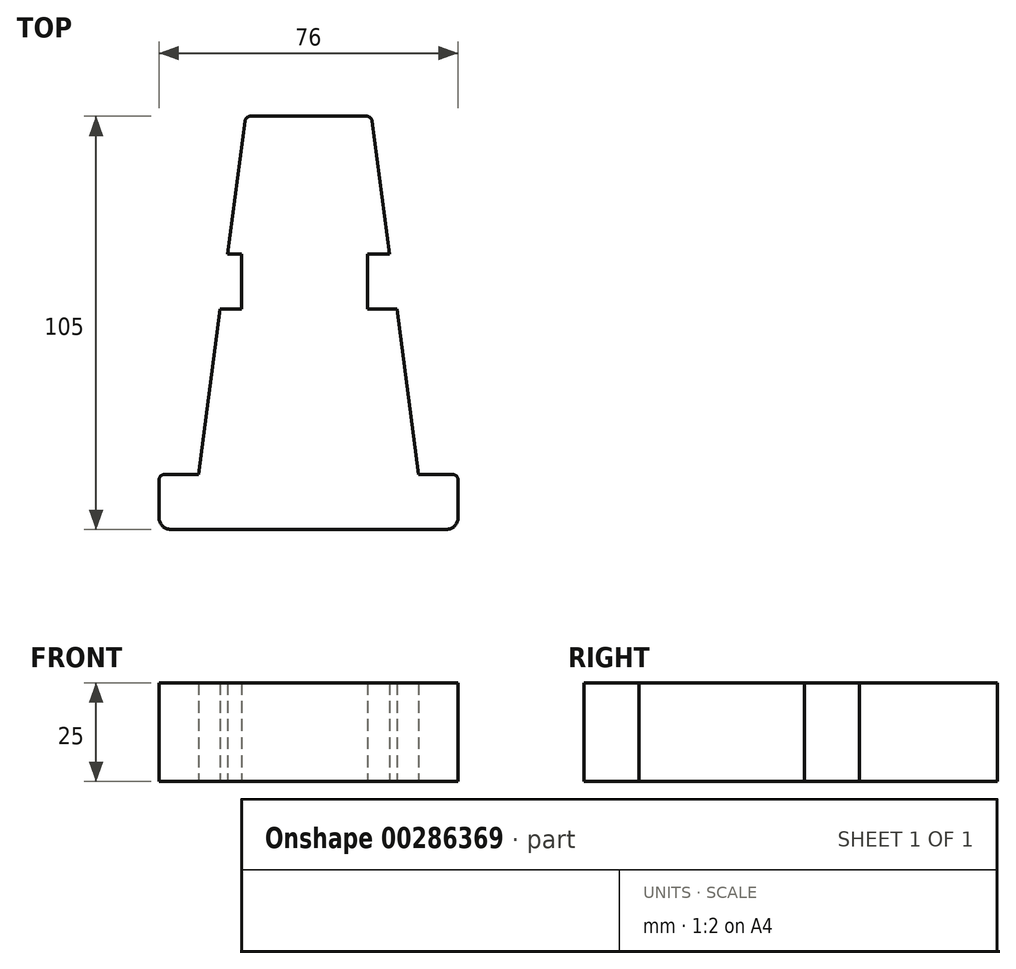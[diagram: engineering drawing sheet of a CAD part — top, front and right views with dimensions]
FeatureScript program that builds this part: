
annotation { "Feature Type Name" : "Feature", "Feature Type Description" : "" }
export const myFeature = defineFeature(function(context is Context, id is Id, definition is map)
    precondition{}
    {
        {
            var Q0;
            Q0=qCreatedBy(makeId("Top.planeOp"),FACE);
            var sketch = newSketch(context, id + "F0", { "sketchPlane" : qUnion([Q0])});
            skLineSegment(sketch, "E0", {"start": v(-46.57, -43.5) * mm, "end": v(-39.57, -43.5) * mm});
            skLineSegment(sketch, "E1", {"start": v(-39.57, -43.5) * mm, "end": v(-27.57, -43.5) * mm});
            skLineSegment(sketch, "E2", {"start": v(-27.57, -43.5) * mm, "end": v(4.43, -43.5) * mm});
            skLineSegment(sketch, "E3", {"start": v(4.43, -43.5) * mm, "end": v(16.43, -43.5) * mm});
            skLineSegment(sketch, "E4", {"start": v(16.43, -43.5) * mm, "end": v(23.43, -43.5) * mm});
            skLineSegment(sketch, "E5", {"start": v(26.43, -40.5) * mm, "end": v(26.43, -31) * mm});
            skLineSegment(sketch, "E6", {"start": v(24.93, -29.5) * mm, "end": v(16.43, -29.5) * mm});
            skLineSegment(sketch, "E7", {"start": v(-49.57, -40.5) * mm, "end": v(-49.57, -31) * mm});
            skLineSegment(sketch, "E8", {"start": v(-48.07, -29.5) * mm, "end": v(-39.57, -29.5) * mm});
            skLineSegment(sketch, "E9", {"start": v(-28.6, 12.5) * mm, "end": v(-28.6, 26.5) * mm});
            skLineSegment(sketch, "E10", {"start": v(3.4, 12.5) * mm, "end": v(3.4, 26.5) * mm});
            skLineSegment(sketch, "E11", {"start": v(-26.23, 61.5) * mm, "end": v(3.09, 61.5) * mm});
            skLineSegment(sketch, "E12", {"start": v(-27.72, 60.2) * mm, "end": v(-32.17, 26.5) * mm});
            skLineSegment(sketch, "E13", {"start": v(4.57, 60.2) * mm, "end": v(9.03, 26.5) * mm});
            skPoint(sketch, "E14.end.orphan", {"position": v(-40.52, 12.5) * mm});
            skPoint(sketch, "E15.end.orphan", {"position": v(15.48, 12.5) * mm});
            skLineSegment(sketch, "E16", {"start": v(-28.6, 26.5) * mm, "end": v(-32.17, 26.5) * mm});
            skLineSegment(sketch, "E17", {"start": v(-28.6, 12.5) * mm, "end": v(-34.02, 12.5) * mm});
            skLineSegment(sketch, "E18.trimOffspring", {"start": v(-34.02, 12.5) * mm, "end": v(-39.57, -29.5) * mm});
            skLineSegment(sketch, "E19", {"start": v(3.4, 26.5) * mm, "end": v(9.03, 26.5) * mm});
            skLineSegment(sketch, "E20", {"start": v(3.4, 12.5) * mm, "end": v(10.88, 12.5) * mm});
            skLineSegment(sketch, "E21.trimOffspring", {"start": v(10.88, 12.5) * mm, "end": v(16.43, -29.5) * mm});
            skPoint(sketch, "E22.visualSharp", {"position": v(-49.57, -43.5) * mm});
            skArc(sketch, "E22.filletArc", {"start": v(-49.57, -40.5) * mm, "mid": v(-48.7, -42.62) * mm, "end": v(-46.57, -43.5) * mm});
            skPoint(sketch, "E23.visualSharp", {"position": v(26.43, -43.5) * mm});
            skArc(sketch, "E23.filletArc", {"start": v(23.43, -43.5) * mm, "mid": v(25.55, -42.62) * mm, "end": v(26.43, -40.5) * mm});
            skPoint(sketch, "E24.visualSharp", {"position": v(-49.57, -29.5) * mm});
            skArc(sketch, "E24.filletArc", {"start": v(-48.07, -29.5) * mm, "mid": v(-49.13, -29.94) * mm, "end": v(-49.57, -31) * mm});
            skPoint(sketch, "E25.visualSharp", {"position": v(26.43, -29.5) * mm});
            skArc(sketch, "E25.filletArc", {"start": v(26.43, -31) * mm, "mid": v(25.99, -29.94) * mm, "end": v(24.93, -29.5) * mm});
            skPoint(sketch, "E26.visualSharp", {"position": v(-27.54, 61.5) * mm});
            skArc(sketch, "E26.filletArc", {"start": v(-26.23, 61.5) * mm, "mid": v(-27.22, 61.13) * mm, "end": v(-27.72, 60.2) * mm});
            skPoint(sketch, "E27.visualSharp", {"position": v(4.4, 61.5) * mm});
            skArc(sketch, "E27.filletArc", {"start": v(4.57, 60.2) * mm, "mid": v(4.08, 61.13) * mm, "end": v(3.09, 61.5) * mm});
            skPoint(sketch, "E28.end.orphan", {"position": v(-11.57, -43.5) * mm});
            skPoint(sketch, "E28.start.orphan", {"position": v(-11.57, 61.5) * mm});
            skLineSegment(sketch, "E29", {"start": v(-11.57, -43.5) * mm, "end": v(-11.57, 61.5) * mm});
            skLineSegment(sketch, "E30", {"start": v(3.4, 26.5) * mm, "end": v(3.09, 61.5) * mm});
            skLineSegment(sketch, "E31", {"start": v(3.4, 12.5) * mm, "end": v(-28.6, 12.5) * mm});
            skSolve(sketch);
        }
        {
            var Q0;
            Q0 = qSketchRegion(id + "F0", true);
            var Q1;
            Q1=makeQuery(id+"F0.imprint","IMPRINT",FACE,{"disambiguationData":[TD([[makeQuery(id+"F0.imprint","IMPRINT",EDGE,{"derivedFrom":sQuery(id+"F0.wireOp",EDGE,"E0")}),1.0]])]});
            extrude(context, id + "F1", {"entities" : qUnion([Q0, Q1]), "depth" : 25 * mm});
        }
    });
